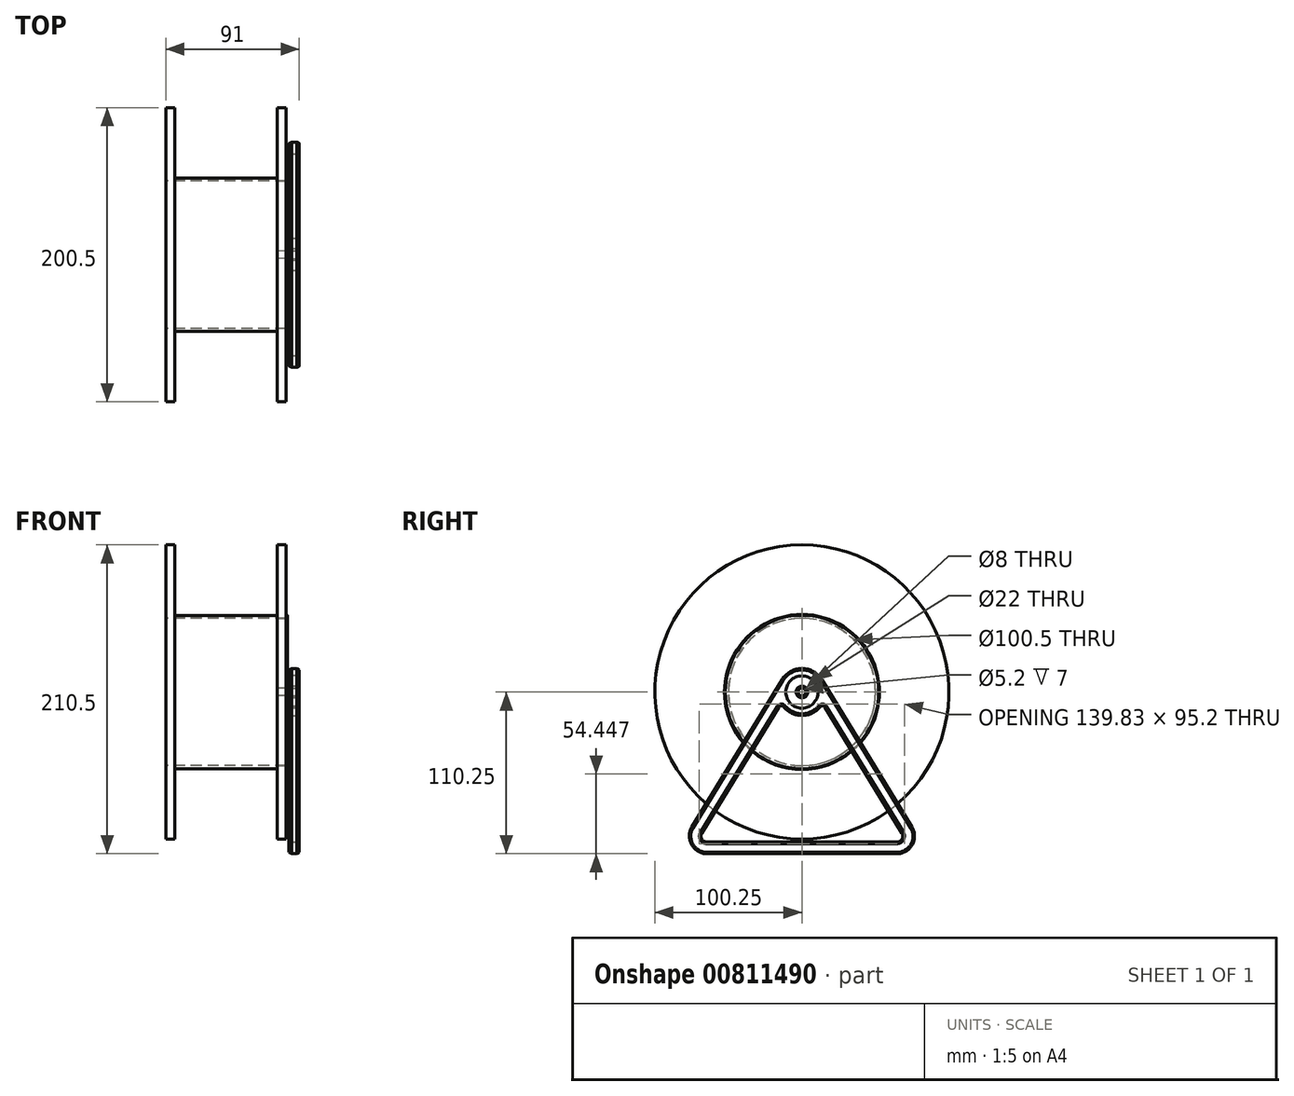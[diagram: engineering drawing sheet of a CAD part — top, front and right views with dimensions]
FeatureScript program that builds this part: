
annotation { "Feature Type Name" : "Feature", "Feature Type Description" : "" }
export const myFeature = defineFeature(function(context is Context, id is Id, definition is map)
    precondition{}
    {
        {
            var Q0;
            Q0=qCreatedBy(makeId("Front.planeOp"),FACE);
            var sketch = newSketch(context, id + "F0", { "sketchPlane" : qUnion([Q0])});
            skLineSegment(sketch, "E0", {"start": v(-41, 50.25) * mm, "end": v(41, 50.25) * mm});
            skLineSegment(sketch, "E1", {"start": v(41, 50.25) * mm, "end": v(41, 100.25) * mm});
            skLineSegment(sketch, "E2", {"start": v(41, 100.25) * mm, "end": v(35, 100.25) * mm});
            skLineSegment(sketch, "E3", {"start": v(35, 100.25) * mm, "end": v(35, 52.25) * mm});
            skLineSegment(sketch, "E4", {"start": v(35, 52.25) * mm, "end": v(-35, 52.25) * mm});
            skLineSegment(sketch, "E5", {"start": v(-35, 52.25) * mm, "end": v(-35, 100.25) * mm});
            skLineSegment(sketch, "E6", {"start": v(-35, 100.25) * mm, "end": v(-41, 100.25) * mm});
            skLineSegment(sketch, "E7", {"start": v(-41, 100.25) * mm, "end": v(-41, 50.25) * mm});
            skLineSegment(sketch, "E8", {"start": v(-137.17, 0) * mm, "end": v(136.18, 0) * mm, "construction": true});
            skSolve(sketch);
        }
        {
            var Q0;
            Q0 = qSketchRegion(id + "F0", true);
            var Q1;
            Q1=sQuery(id+"F0.wireOp",EDGE,"E8");
            revolve(context, id + "F1", {"surfaceOperationType" : NewSurfaceOperationType.NEW, "entities" : qUnion([Q0]), "axis" : qUnion([Q1]), "revolveType" : RevolveType.FULL});
        }
        {
            var Q0;
            Q0=makeQuery(id+"F1.opRevolve","SWEPT_FACE",FACE,{"disambiguationData":[OSD([sQuery(id+"F0.wireOp",EDGE,"E1")])]});
            var sketch = newSketch(context, id + "F2", { "sketchPlane" : qUnion([Q0])});
            skCircle(sketch, "E9", {"center": v(0, 0) * mm, "radius": 11 * mm});
            skCircle(sketch, "E10", {"center": v(0, 0) * mm, "radius": 4 * mm});
            skSolve(sketch);
        }
        {
            var Q0;
            Q0 = qSketchRegion(id + "F2", true);
            extrude(context, id + "F3", {"entities" : qUnion([Q0]), "depth" : 9 * mm, "offsetDistance" : 25 * mm, "hasSecondDirection" : true, "secondDirectionOppositeDirection" : false, "secondDirectionDepth" : 2 * mm});
        }
        {
            var Q0;
            Q0=makeQuery(id+"F1.opRevolve","SWEPT_FACE",FACE,{"disambiguationData":[OSD([sQuery(id+"F0.wireOp",EDGE,"E1")])]});
            var sketch = newSketch(context, id + "F4", { "sketchPlane" : qUnion([Q0])});
            skCircle(sketch, "E11.0", {"center": v(0, 0) * mm, "radius": 50.25 * mm});
            skCircle(sketch, "E12", {"center": v(0, 0) * mm, "radius": 2.5 * mm});
            skSolve(sketch);
        }
        {
            var Q0;
            Q0 = qSketchRegion(id + "F4", true);
            extrude(context, id + "F5", {"entities" : qUnion([Q0]), "oppositeDirection" : true, "depth" : 6 * mm, "offsetDistance" : 25 * mm, "hasDraft" : true, "draftAngle" : 1 * degree, "draftPullDirection" : true});
        }
        {
            var Q0;
            Q0=makeQuery(id+"F5.opExtrude","CAP_FACE",FACE,{"disambiguationData":[OSD([sQuery(id+"F4.wireOp",EDGE,"E11.0"),sQuery(id+"F4.wireOp",EDGE,"E12")])],"isStart":true});
            var sketch = newSketch(context, id + "F6", { "sketchPlane" : qUnion([Q0])});
            skCircle(sketch, "E13.0", {"center": v(0, 0) * mm, "radius": 53.25 * mm});
            skSolve(sketch);
        }
        {
            var Q0;
            Q0 = qSketchRegion(id + "F6", true);
            extrude(context, id + "F7", {"entities" : qUnion([Q0]), "operationType" : NewBodyOperationType.ADD, "depth" : 1 * mm, "offsetDistance" : 25 * mm});
        }
        {
            var Q0;
            Q0=makeQuery(id+"F3.opExtrude","CAP_FACE",FACE,{"disambiguationData":[OSD([sQuery(id+"F2.wireOp",EDGE,"E9"),sQuery(id+"F2.wireOp",EDGE,"E10")])],"isStart":false});
            var sketch = newSketch(context, id + "F8", { "sketchPlane" : qUnion([Q0])});
            skCircle(sketch, "E14.0", {"center": v(0, 0) * mm, "radius": 4 * mm});
            skCircle(sketch, "E15", {"center": v(0, 0) * mm, "radius": 2.6 * mm});
            skSolve(sketch);
        }
        {
            var Q0;
            Q0 = qSketchRegion(id + "F8", true);
            var Q1;
            Q1=makeQuery(id+"F3.opExtrude","CAP_FACE",FACE,{"disambiguationData":[OSD([sQuery(id+"F2.wireOp",EDGE,"E9"),sQuery(id+"F2.wireOp",EDGE,"E10")])],"isStart":true});
            extrude(context, id + "F9", {"entities" : qUnion([Q0]), "endBound" : BoundingType.UP_TO_SURFACE, "oppositeDirection" : true, "depth" : 25 * mm, "endBoundEntityFace" : qUnion([Q1]), "offsetDistance" : 25 * mm});
        }
        {
            var Q0;
            Q0=makeQuery(id+"F3.opExtrude","CAP_FACE",FACE,{"disambiguationData":[OSD([sQuery(id+"F2.wireOp",EDGE,"E9"),sQuery(id+"F2.wireOp",EDGE,"E10")])],"isStart":false});
            var sketch = newSketch(context, id + "F10", { "sketchPlane" : qUnion([Q0])});
            skLineSegment(sketch, "E16", {"start": v(-75, -92) * mm, "end": v(-13.65, 8.35) * mm});
            skArc(sketch, "E17", {"start": v(-13.65, 8.35) * mm, "mid": v(0, 16) * mm, "end": v(13.65, 8.35) * mm});
            skLineSegment(sketch, "E18", {"start": v(13.65, 8.35) * mm, "end": v(75, -92) * mm});
            skArc(sketch, "E19", {"start": v(-75, -92) * mm, "mid": v(-75.23, -104.12) * mm, "end": v(-64.76, -110.25) * mm});
            skArc(sketch, "E20", {"start": v(75, -92) * mm, "mid": v(75.23, -104.12) * mm, "end": v(64.76, -110.25) * mm});
            skLineSegment(sketch, "E21", {"start": v(-64.76, -110.25) * mm, "end": v(64.76, -110.25) * mm});
            skCircle(sketch, "E22.0", {"center": v(0, 0) * mm, "radius": 11 * mm});
            skLineSegment(sketch, "E23.0", {"start": v(-68.17, -96.16) * mm, "end": v(-15.68, -10.3) * mm});
            skLineSegment(sketch, "E23.1", {"start": v(15.68, -10.3) * mm, "end": v(68.17, -96.16) * mm});
            skArc(sketch, "E23.2", {"start": v(68.17, -96.16) * mm, "mid": v(68.25, -100.2) * mm, "end": v(64.76, -102.25) * mm});
            skLineSegment(sketch, "E23.3", {"start": v(-64.76, -102.25) * mm, "end": v(64.76, -102.25) * mm});
            skArc(sketch, "E23.4", {"start": v(-68.17, -96.16) * mm, "mid": v(-68.25, -100.2) * mm, "end": v(-64.76, -102.25) * mm});
            skArc(sketch, "E24", {"start": v(-12.42, -10.09) * mm, "mid": v(0, -16) * mm, "end": v(12.42, -10.09) * mm});
            skPoint(sketch, "E25.visualSharp", {"position": v(-14.05, -7.65) * mm});
            skArc(sketch, "E25.filletArc", {"start": v(-12.42, -10.09) * mm, "mid": v(-14.1, -9.35) * mm, "end": v(-15.68, -10.3) * mm});
            skPoint(sketch, "E26.visualSharp", {"position": v(14.05, -7.65) * mm});
            skArc(sketch, "E26.filletArc", {"start": v(15.68, -10.3) * mm, "mid": v(14.1, -9.35) * mm, "end": v(12.42, -10.09) * mm});
            skSolve(sketch);
        }
        {
            var Q0;
            Q0 = qSketchRegion(id + "F10", true);
            var Q1;
            Q1=makeQuery(id+"F3.opExtrude","CAP_FACE",FACE,{"disambiguationData":[OSD([sQuery(id+"F2.wireOp",EDGE,"E9"),sQuery(id+"F2.wireOp",EDGE,"E10")])],"isStart":true});
            extrude(context, id + "F11", {"entities" : qUnion([Q0]), "endBound" : BoundingType.UP_TO_SURFACE, "oppositeDirection" : true, "depth" : 25 * mm, "endBoundEntityFace" : qUnion([Q1]), "offsetDistance" : 25 * mm});
        }
        {
            var Q0;
            Q0=makeQuery(id+"F7.opExtrude","CAP_EDGE",EDGE,{"disambiguationData":[OSD([sQuery(id+"F6.wireOp",EDGE,"E13.0")])],"isStart":false});
            chamfer(context, id + "F12", {"entities" : qUnion([Q0]), "chamferType" : ChamferType.OFFSET_ANGLE, "width" : 1 * mm, "oppositeDirection" : false, "angle" : 60 * degree, "tangentPropagation" : true});
        }
        {
            var Q0;
            Q0=makeQuery(id+"F11.opExtrude","CAP_EDGE",EDGE,{"disambiguationData":[OSD([sQuery(id+"F10.wireOp",EDGE,"E23.3")])],"isStart":true});
            var Q1;
            Q1=makeQuery(id+"F11.opExtrude","CAP_EDGE",EDGE,{"disambiguationData":[OSD([sQuery(id+"F10.wireOp",EDGE,"E23.3")])],"isStart":false});
            chamfer(context, id + "F13", {"entities" : qUnion([Q0, Q1]), "chamferType" : ChamferType.OFFSET_ANGLE, "width" : 2 * mm, "oppositeDirection" : false, "angle" : 30 * degree, "tangentPropagation" : true});
        }
        {
            var Q0;
            Q0=makeQuery(id+"F11.opExtrude","CAP_EDGE",EDGE,{"disambiguationData":[OSD([sQuery(id+"F10.wireOp",EDGE,"E21")])],"isStart":true});
            var Q1;
            Q1=makeQuery(id+"F11.opExtrude","CAP_EDGE",EDGE,{"disambiguationData":[OSD([sQuery(id+"F10.wireOp",EDGE,"E21")])],"isStart":false});
            chamfer(context, id + "F14", {"entities" : qUnion([Q0, Q1]), "chamferType" : ChamferType.OFFSET_ANGLE, "width" : 1 * mm, "oppositeDirection" : false, "angle" : 60 * degree, "tangentPropagation" : true});
        }
    });
